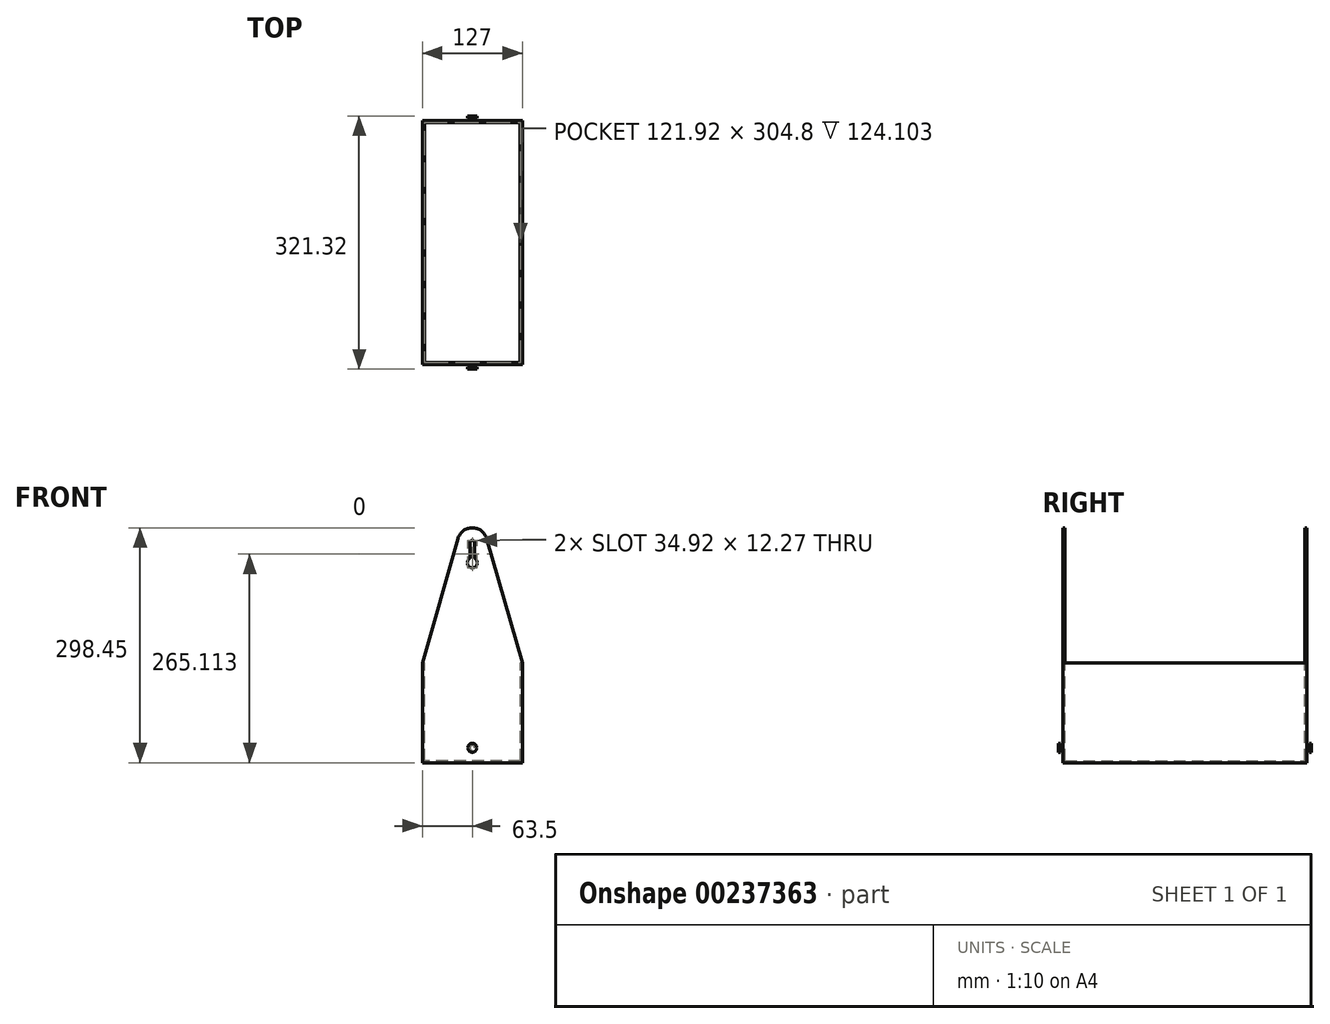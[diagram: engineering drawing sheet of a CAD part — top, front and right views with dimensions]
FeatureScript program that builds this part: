
annotation { "Feature Type Name" : "Feature", "Feature Type Description" : "" }
export const myFeature = defineFeature(function(context is Context, id is Id, definition is map)
    precondition{}
    {
        {
            var Q0;
            Q0=qCreatedBy(makeId("Front.planeOp"),FACE);
            var sketch = newSketch(context, id + "F0", { "sketchPlane" : qUnion([Q0])});
            skLineSegment(sketch, "E0.bottom", {"start": v(63.5, -63.5) * mm, "end": v(-63.5, -63.5) * mm});
            skLineSegment(sketch, "E0.top", {"start": v(63.5, 63.5) * mm, "end": v(-63.5, 63.5) * mm, "construction": true});
            skLineSegment(sketch, "E0.left", {"start": v(63.5, -63.5) * mm, "end": v(63.5, 63.5) * mm});
            skLineSegment(sketch, "E0.right", {"start": v(-63.5, -63.5) * mm, "end": v(-63.5, 63.5) * mm});
            skPoint(sketch, "E0.middle", {"position": v(0, 0) * mm});
            skLineSegment(sketch, "E1", {"start": v(0, 0) * mm, "end": v(0, 215.9) * mm, "construction": true});
            skArc(sketch, "E2", {"start": v(18.31, 221.15) * mm, "mid": v(0, 234.95) * mm, "end": v(-18.31, 221.15) * mm});
            skLineSegment(sketch, "E3", {"start": v(-18.31, 221.15) * mm, "end": v(-63.5, 63.5) * mm});
            skLineSegment(sketch, "E4", {"start": v(18.31, 221.15) * mm, "end": v(63.5, 63.5) * mm});
            skArc(sketch, "E5", {"start": v(3.18, 215.9) * mm, "mid": v(0, 219.08) * mm, "end": v(-3.18, 215.9) * mm});
            skArc(sketch, "E6", {"start": v(-3.17, 196) * mm, "mid": v(0, 184.15) * mm, "end": v(3.17, 196) * mm});
            skLineSegment(sketch, "E7.bottom", {"start": v(3.17, 196) * mm, "end": v(-3.17, 196) * mm, "construction": true});
            skLineSegment(sketch, "E7.top", {"start": v(3.18, 215.9) * mm, "end": v(-3.18, 215.9) * mm, "construction": true});
            skLineSegment(sketch, "E7.left", {"start": v(3.17, 196) * mm, "end": v(3.17, 215.9) * mm});
            skLineSegment(sketch, "E7.right", {"start": v(-3.17, 196) * mm, "end": v(-3.18, 215.9) * mm});
            skPoint(sketch, "E7.middle", {"position": v(0, 205.95) * mm});
            skSolve(sketch);
        }
        {
            var Q0;
            Q0 = qSketchRegion(id + "F0", true);
            extrude(context, id + "F1", {"entities" : qUnion([Q0]), "depth" : 2.54 * mm});
        }
        {
            var Q0;
            Q0=qCreatedBy(makeId("Front.planeOp"),FACE);
            cPlane(context, id + "F2", {"entities" : qUnion([Q0]), "cplaneType" : CPlaneType.OFFSET, "offset" : 152.4 * mm, "oppositeDirection" : true, "width" : 152.4 * mm, "height" : 152.4 * mm});
        }
        {
            var Q0;
            Q0=makeQuery(id+"F1.opExtrude","SWEPT_BODY",BODY,{"disambiguationData":[OSD([sQuery(id+"F0.wireOp",EDGE,"E0.bottom"),sQuery(id+"F0.wireOp",EDGE,"E0.left"),sQuery(id+"F0.wireOp",EDGE,"E0.right"),sQuery(id+"F0.wireOp",EDGE,"E2"),sQuery(id+"F0.wireOp",EDGE,"E3"),sQuery(id+"F0.wireOp",EDGE,"E4"),sQuery(id+"F0.wireOp",EDGE,"E5"),sQuery(id+"F0.wireOp",EDGE,"E6"),sQuery(id+"F0.wireOp",EDGE,"E7.left"),sQuery(id+"F0.wireOp",EDGE,"E7.right")])]});
            var Q1;
            Q1=qCreatedBy(id+"F2.planeOp",FACE);
            mirror(context, id + "F3", {"entities" : qUnion([Q0]), "mirrorPlane" : qUnion([Q1])});
        }
        {
            var Q0;
            Q0=makeQuery(id+"F3.opPattern","COPY",FACE,{"derivedFrom":makeQuery(id+"F1.opExtrude","CAP_FACE",FACE,{"disambiguationData":[OSD([sQuery(id+"F0.wireOp",EDGE,"E0.bottom"),sQuery(id+"F0.wireOp",EDGE,"E0.left"),sQuery(id+"F0.wireOp",EDGE,"E0.right"),sQuery(id+"F0.wireOp",EDGE,"E2"),sQuery(id+"F0.wireOp",EDGE,"E3"),sQuery(id+"F0.wireOp",EDGE,"E4"),sQuery(id+"F0.wireOp",EDGE,"E5"),sQuery(id+"F0.wireOp",EDGE,"E6"),sQuery(id+"F0.wireOp",EDGE,"E7.left"),sQuery(id+"F0.wireOp",EDGE,"E7.right")])],"isStart":true}),"instanceName":"1"});
            var sketch = newSketch(context, id + "F4", { "sketchPlane" : qUnion([Q0])});
            skLineSegment(sketch, "E8.0", {"start": v(-63.5, -63.5) * mm, "end": v(-63.5, 63.5) * mm});
            skLineSegment(sketch, "E9.0", {"start": v(63.5, -63.5) * mm, "end": v(-63.5, -63.5) * mm});
            skLineSegment(sketch, "E10.0", {"start": v(63.5, -63.5) * mm, "end": v(63.5, 63.5) * mm});
            skLineSegment(sketch, "E11", {"start": v(-63.5, 63.5) * mm, "end": v(63.5, 63.5) * mm});
            skSolve(sketch);
        }
        {
            var Q0;
            Q0 = qSketchRegion(id + "F4", true);
            var Q1;
            Q1=makeQuery(id+"F1.opExtrude","CAP_FACE",FACE,{"disambiguationData":[OSD([sQuery(id+"F0.wireOp",EDGE,"E0.bottom"),sQuery(id+"F0.wireOp",EDGE,"E0.left"),sQuery(id+"F0.wireOp",EDGE,"E0.right"),sQuery(id+"F0.wireOp",EDGE,"E2"),sQuery(id+"F0.wireOp",EDGE,"E3"),sQuery(id+"F0.wireOp",EDGE,"E4"),sQuery(id+"F0.wireOp",EDGE,"E5"),sQuery(id+"F0.wireOp",EDGE,"E6"),sQuery(id+"F0.wireOp",EDGE,"E7.left"),sQuery(id+"F0.wireOp",EDGE,"E7.right")])],"isStart":true});
            extrude(context, id + "F5", {"entities" : qUnion([Q0]), "operationType" : NewBodyOperationType.ADD, "endBound" : BoundingType.UP_TO_SURFACE, "endBoundEntityFace" : qUnion([Q1]), "depth" : 25.4 * mm});
        }
        {
            var Q0;
            Q0=makeQuery(id+"F5.opExtrude","SWEPT_FACE",FACE,{"disambiguationData":[OSD([sQuery(id+"F4.wireOp",EDGE,"E11")])]});
            shell(context, id + "F6", {"entities" : qUnion([Q0]), "thickness" : 2.54 * mm});
        }
        {
            var Q0;
            Q0=makeQuery(id+"F1.opExtrude","CAP_FACE",FACE,{"disambiguationData":[OSD([sQuery(id+"F0.wireOp",EDGE,"E0.bottom"),sQuery(id+"F0.wireOp",EDGE,"E0.left"),sQuery(id+"F0.wireOp",EDGE,"E0.right"),sQuery(id+"F0.wireOp",EDGE,"E2"),sQuery(id+"F0.wireOp",EDGE,"E3"),sQuery(id+"F0.wireOp",EDGE,"E4"),sQuery(id+"F0.wireOp",EDGE,"E5"),sQuery(id+"F0.wireOp",EDGE,"E6"),sQuery(id+"F0.wireOp",EDGE,"E7.left"),sQuery(id+"F0.wireOp",EDGE,"E7.right")])],"isStart":false});
            var sketch = newSketch(context, id + "F7", { "sketchPlane" : qUnion([Q0])});
            skCircle(sketch, "E12", {"center": v(0, -44.45) * mm, "radius": 3.18 * mm});
            skSolve(sketch);
        }
        {
            var Q0;
            Q0 = qSketchRegion(id + "F7", true);
            extrude(context, id + "F8", {"entities" : qUnion([Q0]), "depth" : 3.17 * mm});
        }
        {
            var Q0;
            Q0=makeQuery(id+"F8.opExtrude","CAP_FACE",FACE,{"disambiguationData":[OSD([sQuery(id+"F7.wireOp",EDGE,"E12")])],"isStart":false});
            var sketch = newSketch(context, id + "F9", { "sketchPlane" : qUnion([Q0])});
            skCircle(sketch, "E13", {"center": v(0, -44.45) * mm, "radius": 5.71 * mm});
            skSolve(sketch);
        }
        {
            var Q0;
            Q0 = qSketchRegion(id + "F9", true);
            extrude(context, id + "F10", {"entities" : qUnion([Q0]), "operationType" : NewBodyOperationType.ADD, "depth" : 2.54 * mm});
        }
        {
            var Q0;
            Q0=makeQuery(id+"F10.opExtrude","SWEPT_BODY",BODY,{"disambiguationData":[OSD([sQuery(id+"F9.wireOp",EDGE,"E13")])]});
            var Q1;
            Q1=makeQuery(id+"F8.opExtrude","SWEPT_BODY",BODY,{"disambiguationData":[OSD([sQuery(id+"F7.wireOp",EDGE,"E12")])]});
            var Q2;
            Q2=qCreatedBy(id+"F2.planeOp",FACE);
            mirror(context, id + "F11", {"operationType" : NewBodyOperationType.ADD, "entities" : qUnion([Q0, Q1]), "mirrorPlane" : qUnion([Q2])});
        }
    });
